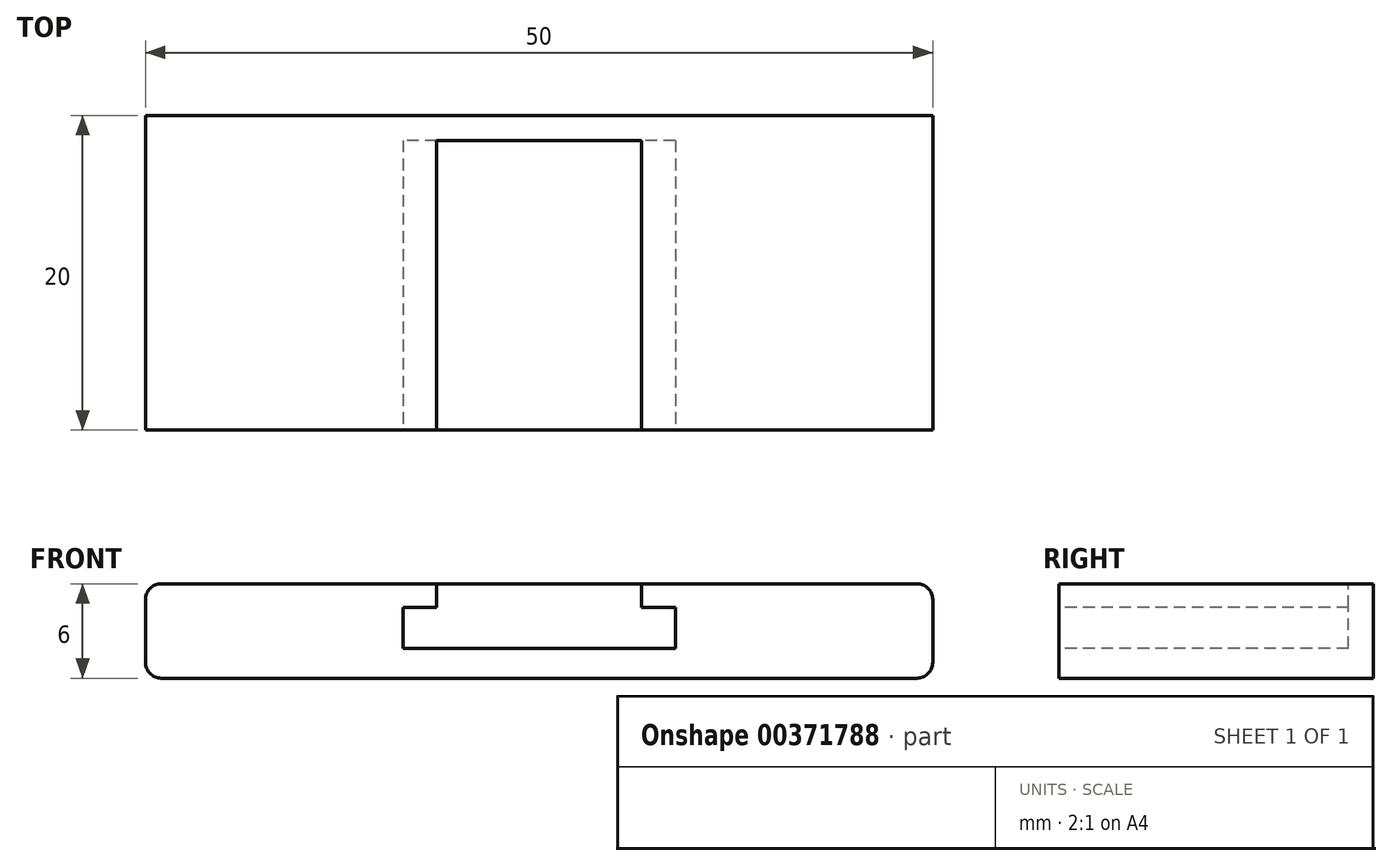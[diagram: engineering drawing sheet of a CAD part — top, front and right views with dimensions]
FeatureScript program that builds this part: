
annotation { "Feature Type Name" : "Feature", "Feature Type Description" : "" }
export const myFeature = defineFeature(function(context is Context, id is Id, definition is map)
    precondition{}
    {
        {
            var Q0;
            Q0=qCreatedBy(makeId("Top.planeOp"),FACE);
            var sketch = newSketch(context, id + "F0", { "sketchPlane" : qUnion([Q0])});
            skLineSegment(sketch, "E0", {"start": v(0, 0) * mm, "end": v(50, 0) * mm});
            skLineSegment(sketch, "E1", {"start": v(50, 0) * mm, "end": v(50, 20) * mm});
            skLineSegment(sketch, "E2", {"start": v(50, 20) * mm, "end": v(0, 20) * mm});
            skLineSegment(sketch, "E3", {"start": v(0, 20) * mm, "end": v(0, 0) * mm});
            skSolve(sketch);
        }
        {
            var Q0;
            Q0=makeQuery(id+"F0.imprint","IMPRINT",FACE,{"disambiguationData":[TD([[makeQuery(id+"F0.imprint","IMPRINT",EDGE,{"derivedFrom":sQuery(id+"F0.wireOp",EDGE,"E0")}),1.0]])]});
            extrude(context, id + "F1", {"entities" : qUnion([Q0]), "depth" : 6 * mm, "offsetDistance" : 25 * mm});
        }
        {
            var Q0;
            Q0=makeQuery(id+"F1.opExtrude","SWEPT_FACE",FACE,{"disambiguationData":[OSD([sQuery(id+"F0.wireOp",EDGE,"E0")])]});
            var sketch = newSketch(context, id + "F2", { "sketchPlane" : qUnion([Q0])});
            skLineSegment(sketch, "E4.bottom", {"start": v(16.35, 4.5) * mm, "end": v(33.65, 4.5) * mm});
            skLineSegment(sketch, "E4.top", {"start": v(16.35, 1.9) * mm, "end": v(33.65, 1.9) * mm});
            skLineSegment(sketch, "E4.left", {"start": v(16.35, 4.5) * mm, "end": v(16.35, 1.9) * mm});
            skLineSegment(sketch, "E4.right", {"start": v(33.65, 4.5) * mm, "end": v(33.65, 1.9) * mm});
            skLineSegment(sketch, "E5.bottom", {"start": v(18.5, 6) * mm, "end": v(31.5, 6) * mm});
            skLineSegment(sketch, "E5.top", {"start": v(18.5, 4.5) * mm, "end": v(31.5, 4.5) * mm});
            skLineSegment(sketch, "E5.left", {"start": v(18.5, 6) * mm, "end": v(18.5, 4.5) * mm});
            skLineSegment(sketch, "E5.right", {"start": v(31.5, 6) * mm, "end": v(31.5, 4.5) * mm});
            skLineSegment(sketch, "E6", {"start": v(25, 0) * mm, "end": v(25, 1.9) * mm, "construction": true});
            skPoint(sketch, "E7", {"position": v(25, 6) * mm});
            skSolve(sketch);
        }
        {
            var Q0;
            Q0=makeQuery(id+"F2.imprint","IMPRINT",FACE,{"disambiguationData":[TD([[makeQuery(id+"F2.imprint","IMPRINT",EDGE,{"derivedFrom":sQuery(id+"F2.wireOp",EDGE,"E4.top")}),1.0]])]});
            var Q1;
            Q1=makeQuery(id+"F2.imprint","IMPRINT",FACE,{"disambiguationData":[TD([[makeQuery(id+"F2.imprint","IMPRINT",EDGE,{"derivedFrom":sQuery(id+"F2.wireOp",EDGE,"E5.bottom")}),-1.0]])]});
            var Q2;
            Q2=makeQuery(id+"F1.opExtrude","SWEPT_FACE",FACE,{"disambiguationData":[OSD([sQuery(id+"F0.wireOp",EDGE,"E2")])]});
            extrude(context, id + "F3", {"entities" : qUnion([Q0, Q1]), "operationType" : NewBodyOperationType.REMOVE, "endBound" : BoundingType.UP_TO_SURFACE, "oppositeDirection" : true, "depth" : 25 * mm, "endBoundEntityFace" : qUnion([Q2]), "hasOffset" : true, "offsetDistance" : 1.6 * mm});
        }
        {
            var Q0;
            Q0=makeQuery(id+"F1.opExtrude","CAP_EDGE",EDGE,{"disambiguationData":[OSD([sQuery(id+"F0.wireOp",EDGE,"E1")])],"isStart":false});
            var Q1;
            Q1=makeQuery(id+"F1.opExtrude","CAP_EDGE",EDGE,{"disambiguationData":[OSD([sQuery(id+"F0.wireOp",EDGE,"E1")])],"isStart":true});
            var Q2;
            Q2=makeQuery(id+"F1.opExtrude","CAP_EDGE",EDGE,{"disambiguationData":[OSD([sQuery(id+"F0.wireOp",EDGE,"E3")])],"isStart":true});
            var Q3;
            Q3=makeQuery(id+"F1.opExtrude","CAP_EDGE",EDGE,{"disambiguationData":[OSD([sQuery(id+"F0.wireOp",EDGE,"E3")])],"isStart":false});
            fillet(context, id + "F4", {"entities" : qUnion([Q0, Q1, Q2, Q3]), "radius" : 1 * mm, "tangentPropagation" : true, "allowEdgeOverflow" : false});
        }
    });
